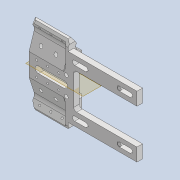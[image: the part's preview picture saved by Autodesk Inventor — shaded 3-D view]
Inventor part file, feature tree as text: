
AUTODESK INVENTOR PART (.ipt)
format: ipt  version: 2020 (Build 240168000, 168)  size: 695,808 bytes
history: native  units: mm
features: reference x19, projected_geometry x19, sketch x16, extrude x14, thicken_offset x13, fillet x7, other x7, mirror x4, plane x3, chamfer x3, hole x2
ambient origin geometry x8: Origin, YZ Plane, XZ Plane, XY Plane, X Axis, Y Axis, Z Axis, Center Point
bodies: Solid1 (feature_tree)
feature tree (107):
  sketch  "Sketch1"  dims[d0=5.0mm d1=7.0mm]
  plane  "Work Plane1"
  extrude  "Extrusion1"  Depth=7.0mm
  sketch  "Sketch2"  dims[d2=5.0mm d3=7.0mm]
  plane  "Work Plane2"
  extrude  "Extrusion2"  Depth=7.0mm
  hole  "Hole1"  [1 undecoded]
  plane  "Work Plane3"
  mirror  "Mirror1"
  extrude  "Extrusion3"  Depth=10.0mm
  thicken_offset  "Thicken1"
  thicken_offset  "Thicken2"
  thicken_offset  "Thicken3"
  extrude  "Extrusion4"  Depth=10.0mm
  extrude  "Extrusion5"  Depth=20.0mm TaperAngle=0.0deg
  thicken_offset  "Thicken4"
  thicken_offset  "Thicken5"
  extrude  "Extrusion6"  Depth=1.0mm
  extrude  "Extrusion7"  Depth=1.0mm
  fillet  "Fillet2"  Radius=1.0mm
  fillet  "Fillet3"  Radius=1.0mm
  fillet  "Fillet4"  Radius=2.9mm
  thicken_offset  "Thicken6"
  thicken_offset  "Thicken7"
  fillet  "Fillet5"  Radius=1.45mm
  chamfer  "Chamfer1"  Distance=21.5mm
  extrude  "Extrusion8"  Depth=1.0mm
  fillet  "Fillet6"  Radius=1.0mm
  chamfer  "Chamfer2"  Distance=20.0mm
  extrude  "Extrusion9"  Depth=0.5mm
  fillet  "Fillet7"  Radius=0.5mm
  mirror  "Mirror2"
  hole  "Hole2"  [1 undecoded]
  extrude  "Extrusion10"  Depth=10.0mm
  extrude  "Extrusion11"  Depth=10.0mm
  mirror  "Mirror3"
  extrude  "Extrusion12"  Depth=1.0mm
  mirror  "Mirror4"
  chamfer  "Chamfer3"  Distance=0.5mm
  fillet  "Fillet8"  Radius=0.5mm
  thicken_offset  "Thicken8"
  thicken_offset  "Thicken9"
  thicken_offset  "Thicken10"
  thicken_offset  "Thicken11"
  thicken_offset  "Thicken12"
  thicken_offset  "Thicken13"
  extrude  "Extrusion14"  Depth=10.0mm
  extrude  "Extrusion15"  Depth=10.0mm
  reference  "Reference1"
  reference  "Reference2"
  reference  "Reference3"
  reference  "Reference4"
  reference  "Reference5"
  reference  "Reference6"
  reference  "Reference7"
  reference  "Reference8"
  reference  "Reference9"
  reference  "Reference10"
  reference  "Reference11"
  reference  "Reference12"
  reference  "Reference13"
  reference  "Reference14"
  projected_geometry  "Projected Loop1"
  sketch  "Sketch3"  dims[d4=3.0mm d5=21.0mm]
  reference  "Reference15"
  reference  "Reference16"
  reference  "Reference17"
  sketch  "Sketch4"  dims[d6=10.0mm d7=0.0mm d8=2.0mm]
  projected_geometry  "Projected Loop2"
  projected_geometry  "Projected Loop3"
  sketch  "Sketch5"  dims[d9=10.0mm d10=0.0mm]
  projected_geometry  "Projected Loop4"
  sketch  "Sketch6"  dims[d11=1.1mm d12=6.0mm d13=4.0mm d14=2.0mm d15=90.0deg d16=10.0mm d17=0.0mm d18=2.0mm]
  projected_geometry  "Projected Loop5"
  projected_geometry  "Projected Loop6"
  projected_geometry  "Projected Loop7"
  sketch  "Sketch7"  dims[d19=2.0mm d20=20.0mm d21=0.0mm]
  projected_geometry  "Projected Loop8"
  projected_geometry  "Projected Loop9"
  sketch  "Sketch8"  dims[d22=1.0mm d23=1.0mm]
  projected_geometry  "Projected Loop10"
  sketch  "Sketch9"  dims[d24=1.0mm d25=1.0mm d26=1.0mm d27=1.0mm d28=2.9mm d29=1.45mm]
  projected_geometry  "Projected Loop11"
  projected_geometry  "Projected Loop12"
  sketch  "Sketch10"  dims[d30=2.9mm]
  projected_geometry  "Projected Loop13"
  sketch  "Sketch11"  dims[d31=12.0mm d32=21.5mm d33=0.0mm]
  projected_geometry  "Projected Loop14"
  sketch  "Sketch12"  dims[d35=1.0mm d36=1.0mm d37=1.0mm]
  projected_geometry  "Projected Loop15"
  sketch  "Sketch13"  dims[d38=1.0mm d39=20.0mm d40=0.0mm]
  projected_geometry  "Projected Loop16"
  sketch  "Sketch14"  dims[d41=0.5mm d42=0.5mm d43=0.5mm]
  projected_geometry  "Projected Loop17"
  sketch  "Sketch15"  dims[d44=0.5mm d45=20.0mm d46=0.0mm]
  reference  "Reference18"
  reference  "Reference19"
  projected_geometry  "Projected Loop18"
  sketch  "Sketch16"  dims[d47=0.1mm d48=0.0mm d49=0.4mm d50=0.6mm d51=1.0mm d52=0.5mm d53=0.5mm d54=0.5mm d55=0.5mm d56=3.0mm d57=1.5mm d58=2.0mm d59=45.0deg d60=2.0mm d61=0.0mm d62=1.0mm d63=1.5mm d64=2.0mm d65=45.0deg d66=3.5mm d67=3.5mm d68=1.5mm d69=30.0mm d70=0.0mm d71=1.0mm d72=4.0mm d73=6.0mm d74=6.0mm d75=4.0mm d76=4.0mm d77=4.0mm d78=4.0mm d79=4.0mm d80=4.0mm d81=1.1mm d82=6.0mm d83=4.0mm d84=2.0mm d85=90.0deg d86=10.0mm d87=0.0mm d88=7.0mm d89=3.5mm d90=30.0mm d91=0.0mm d92=4.0mm d93=1.0mm d94=2.0mm d95=30.0mm d96=0.0mm d97=5.0mm d98=8.0mm d99=2.0mm d100=2.0mm d101=30.0mm d102=0.0mm d103=2.0mm d104=2.0mm d105=45.0deg d106=1.5mm d107=30.0mm d108=30.0mm d109=30.0mm d110=30.0mm d111=1.0mm d112=1.0mm d113=1.0mm d114=1.0mm d115=1.0mm d116=1.0mm d117=1.0mm d118=1.0mm d119=6.0mm d120=2.4mm d121=6.0mm d122=2.4mm d123=6.0mm d124=2.4mm d125=6.0mm d126=2.4mm d129=10.0mm d130=0.0mm d131=2.0mm d132=2.0mm d133=10.0mm d134=0.0mm]
  projected_geometry  "Projected Loop19"
  parser-record x2  (decoder bookkeeping rows leaked as tree rows — omitted from the tree; the rows remain in map.json)
  other  "tip_3_n_ass.iam"
  other  "end_shell_n_1:1"
  other  "bl_tube_ass_2:1"
  other  "bl_tube_hn_1:1"
  other  "tip_3_n_base_ass.iam"
note: 2 required parameter values undecoded (feature->parameter linkage not recoverable at this tier; creation-order binding heuristic only, values carry confidence <= 0.55)
note: 2 file-system paths scrubbed to <path> (originals preserved in map.json)
